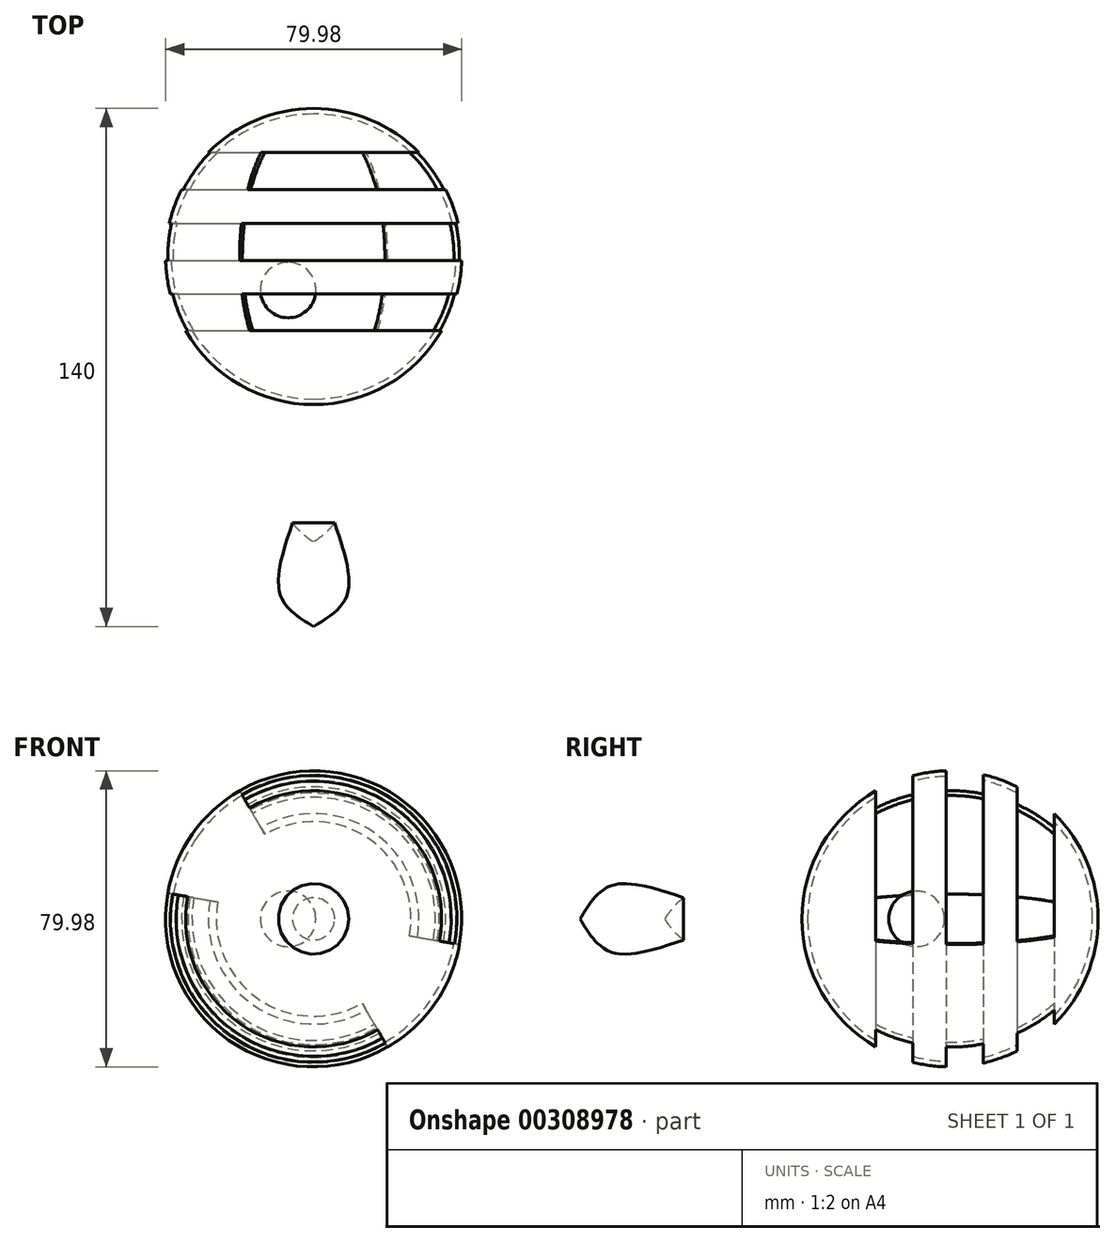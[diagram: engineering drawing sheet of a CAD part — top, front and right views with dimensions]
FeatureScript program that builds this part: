
annotation { "Feature Type Name" : "Feature", "Feature Type Description" : "" }
export const myFeature = defineFeature(function(context is Context, id is Id, definition is map)
    precondition{}
    {
        {
            var Q0;
            Q0=qCreatedBy(makeId("Top.planeOp"),FACE);
            var sketch = newSketch(context, id + "F0", { "sketchPlane" : qUnion([Q0])});
            skArc(sketch, "E0", {"start": v(0, -6.9) * mm, "mid": v(40, 33.1) * mm, "end": v(0, 73.1) * mm});
            skArc(sketch, "E1", {"start": v(0, -5.4) * mm, "mid": v(38.5, 33.1) * mm, "end": v(0, 71.6) * mm});
            skLineSegment(sketch, "E2", {"start": v(0, -6.9) * mm, "end": v(0, -66.9) * mm});
            skFitSpline(sketch, "E3", {"points": [v(10.1, -5.6) * mm, v(5.7, -38.9) * mm, v(-25.14, -52.42) * mm], "startDerivative": vector(4.38, -76.52) * mm, "endDerivative": vector(-74.84, -17.12) * mm});
            skFitSpline(sketch, "E4", {"points": [v(5.7, -38.9) * mm, v(9.01, -58.35) * mm, v(0, -66.9) * mm], "startDerivative": vector(13.3, -39.22) * mm, "endDerivative": vector(-26.2, -15.86) * mm});
            skLineSegment(sketch, "E5", {"start": v(0, -6.9) * mm, "end": v(0, 73.1) * mm});
            skSolve(sketch);
        }
        {
            var Q0;
            {var subQ0=sQuery(id+"F0.wireOp",EDGE,"E1");Q0=makeQuery(id+"F0.imprint","IMPRINT",FACE,{"disambiguationData":[TD([[makeQuery(id+"F0.imprint","IMPRINT",EDGE,{"derivedFrom":subQ0}),-1.0]])]});}
            var Q1;
            {var subQ0=sQuery(id+"F0.wireOp",EDGE,"E2");Q1=makeQuery(id+"F0.imprint","IMPRINT",FACE,{"disambiguationData":[TD([[makeQuery(id+"F0.imprint","IMPRINT",EDGE,{"derivedFrom":subQ0}),1.0]])]});}
            var Q2;
            Q2=sQuery(id+"F0.wireOp",EDGE,"E2");
            revolve(context, id + "F1", {"entities" : qUnion([Q0, Q1]), "axis" : qUnion([Q2]), "revolveType" : RevolveType.FULL});
        }
        {
            var Q0;
            Q0=qCreatedBy(makeId("Right.planeOp"),FACE);
            var sketch = newSketch(context, id + "F2", { "sketchPlane" : qUnion([Q0])});
            skLineSegment(sketch, "E6.bottom", {"start": v(61.23, 50.23) * mm, "end": v(51.23, 50.23) * mm});
            skLineSegment(sketch, "E6.top", {"start": v(61.23, -59.77) * mm, "end": v(51.23, -59.77) * mm});
            skLineSegment(sketch, "E6.left", {"start": v(61.23, 50.23) * mm, "end": v(61.23, 9.73) * mm});
            skLineSegment(sketch, "E6.right", {"start": v(51.23, 50.23) * mm, "end": v(51.23, 9.73) * mm});
            skLineSegment(sketch, "E7.bottom", {"start": v(42.02, 50.7) * mm, "end": v(32.02, 50.7) * mm});
            skLineSegment(sketch, "E7.top", {"start": v(42.02, -59.3) * mm, "end": v(32.02, -59.3) * mm});
            skLineSegment(sketch, "E7.left", {"start": v(42.02, 50.7) * mm, "end": v(42.02, 9.73) * mm});
            skLineSegment(sketch, "E7.right", {"start": v(32.02, 50.7) * mm, "end": v(32.02, 9.73) * mm});
            skLineSegment(sketch, "E8.bottom", {"start": v(23.05, 50.7) * mm, "end": v(13.05, 50.7) * mm});
            skLineSegment(sketch, "E8.top", {"start": v(23.05, -59.3) * mm, "end": v(13.05, -59.3) * mm});
            skLineSegment(sketch, "E8.left", {"start": v(23.05, 50.7) * mm, "end": v(23.05, 9.73) * mm});
            skLineSegment(sketch, "E8.right", {"start": v(13.05, 50.7) * mm, "end": v(13.05, 9.73) * mm});
            skLineSegment(sketch, "E9.bottom", {"start": v(61.23, 9.73) * mm, "end": v(51.23, 9.73) * mm});
            skLineSegment(sketch, "E9.top", {"start": v(61.23, -10.91) * mm, "end": v(51.23, -10.91) * mm});
            skLineSegment(sketch, "E10.trimOffspring", {"start": v(23.05, 9.73) * mm, "end": v(13.05, 9.73) * mm});
            skLineSegment(sketch, "E11.trimOffspring", {"start": v(23.05, -10.91) * mm, "end": v(13.05, -10.91) * mm});
            skLineSegment(sketch, "E12.trimOffspring", {"start": v(42.02, 9.73) * mm, "end": v(32.02, 9.73) * mm});
            skLineSegment(sketch, "E13.trimOffspring", {"start": v(42.02, -10.91) * mm, "end": v(32.02, -10.91) * mm});
            skLineSegment(sketch, "E14.trimOffspring", {"start": v(61.23, -10.91) * mm, "end": v(61.23, -59.77) * mm});
            skLineSegment(sketch, "E15.trimOffspring", {"start": v(51.23, -10.91) * mm, "end": v(51.23, -59.77) * mm});
            skLineSegment(sketch, "E16.trimOffspring", {"start": v(42.02, -10.91) * mm, "end": v(42.02, -59.3) * mm});
            skLineSegment(sketch, "E17.trimOffspring", {"start": v(32.02, -10.91) * mm, "end": v(32.02, -59.3) * mm});
            skLineSegment(sketch, "E18.trimOffspring", {"start": v(23.05, -10.91) * mm, "end": v(23.05, -59.3) * mm});
            skLineSegment(sketch, "E19.trimOffspring", {"start": v(13.05, -10.91) * mm, "end": v(13.05, -59.3) * mm});
            skLineSegment(sketch, "E20", {"start": v(0, 0) * mm, "end": v(73.3, 0) * mm});
            skSolve(sketch);
        }
        {
            var Q0;
            Q0=makeQuery(id+"F2.imprint","IMPRINT",FACE,{"disambiguationData":[TD([[makeQuery(id+"F2.imprint","IMPRINT",EDGE,{"derivedFrom":sQuery(id+"F2.wireOp",EDGE,"E8.bottom")}),1.0]])]});
            var Q1;
            Q1=makeQuery(id+"F2.imprint","IMPRINT",FACE,{"disambiguationData":[TD([[makeQuery(id+"F2.imprint","IMPRINT",EDGE,{"derivedFrom":sQuery(id+"F2.wireOp",EDGE,"E7.bottom")}),1.0]])]});
            var Q2;
            Q2=makeQuery(id+"F2.imprint","IMPRINT",FACE,{"disambiguationData":[TD([[makeQuery(id+"F2.imprint","IMPRINT",EDGE,{"derivedFrom":sQuery(id+"F2.wireOp",EDGE,"E6.bottom")}),1.0]])]});
            var Q3;
            Q3=makeQuery(id+"F2.imprint","IMPRINT",FACE,{"disambiguationData":[TD([[makeQuery(id+"F2.imprint","IMPRINT",EDGE,{"derivedFrom":sQuery(id+"F2.wireOp",EDGE,"E6.top")}),-1.0]])]});
            var Q4;
            Q4=makeQuery(id+"F2.imprint","IMPRINT",FACE,{"disambiguationData":[TD([[makeQuery(id+"F2.imprint","IMPRINT",EDGE,{"derivedFrom":sQuery(id+"F2.wireOp",EDGE,"E7.top")}),-1.0]])]});
            var Q5;
            Q5=makeQuery(id+"F2.imprint","IMPRINT",FACE,{"disambiguationData":[TD([[makeQuery(id+"F2.imprint","IMPRINT",EDGE,{"derivedFrom":sQuery(id+"F2.wireOp",EDGE,"E8.top")}),-1.0]])]});
            var Q6;
            Q6=sQuery(id+"F2.wireOp",EDGE,"E20");
            revolve(context, id + "F3", {"operationType" : NewBodyOperationType.REMOVE, "entities" : qUnion([Q0, Q1, Q2, Q3, Q4, Q5]), "axis" : qUnion([Q6]), "revolveType" : RevolveType.TWO_DIRECTIONS, "angle" : 100 * degree, "angleBack" : 330 * degree});
        }
        {
            var Q0;
            Q0=qCreatedBy(makeId("Top.planeOp"),FACE);
            var sketch = newSketch(context, id + "F4", { "sketchPlane" : qUnion([Q0])});
            skArc(sketch, "E21", {"start": v(-6.9, 16.55) * mm, "mid": v(0.6, 24.05) * mm, "end": v(-6.9, 31.55) * mm});
            skLineSegment(sketch, "E22", {"start": v(-6.9, 24.05) * mm, "end": v(-6.9, 31.55) * mm});
            skLineSegment(sketch, "E23", {"start": v(-6.9, 24.05) * mm, "end": v(-6.9, 16.55) * mm});
            skSolve(sketch);
        }
        {
            var Q0;
            Q0=makeQuery(id+"F4.imprint","IMPRINT",FACE,{"disambiguationData":[TD([[makeQuery(id+"F4.imprint","IMPRINT",EDGE,{"derivedFrom":sQuery(id+"F4.wireOp",EDGE,"E21")}),1.0]])]});
            var Q1;
            Q1=sQuery(id+"F4.wireOp",EDGE,"E22");
            revolve(context, id + "F5", {"entities" : qUnion([Q0]), "axis" : qUnion([Q1]), "revolveType" : RevolveType.FULL});
        }
    });
